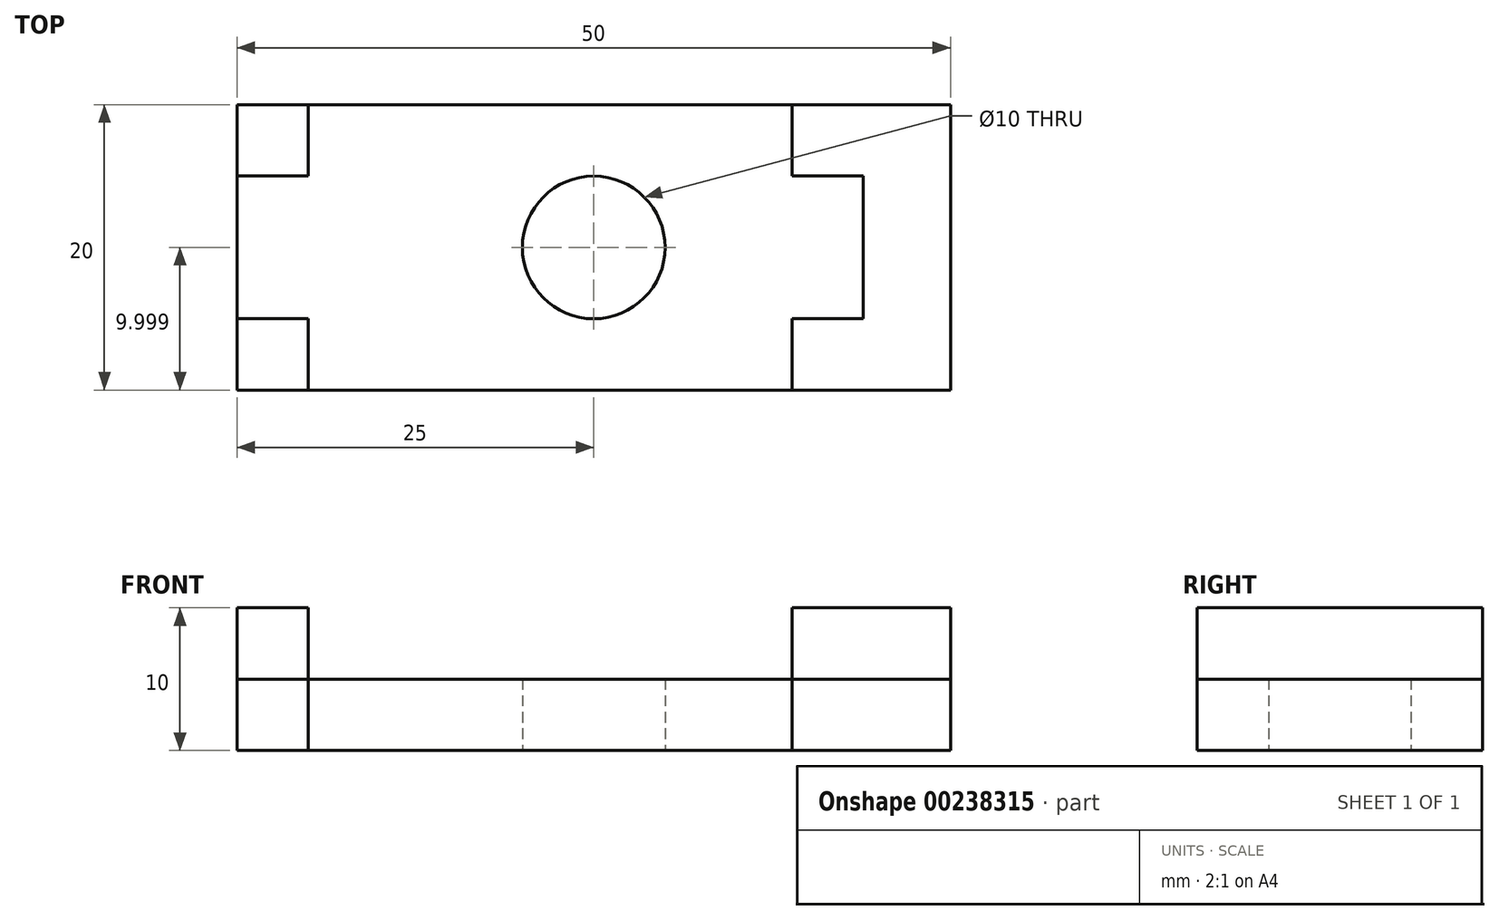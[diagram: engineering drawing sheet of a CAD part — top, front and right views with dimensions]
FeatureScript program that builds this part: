
annotation { "Feature Type Name" : "Feature", "Feature Type Description" : "" }
export const myFeature = defineFeature(function(context is Context, id is Id, definition is map)
    precondition{}
    {
        {
            var Q0;
            Q0=qCreatedBy(makeId("Top.planeOp"),FACE);
            var sketch = newSketch(context, id + "F0", { "sketchPlane" : qUnion([Q0])});
            skLineSegment(sketch, "E0.bottom", {"start": v(-21.46, 12.43) * mm, "end": v(28.54, 12.43) * mm});
            skLineSegment(sketch, "E0.top", {"start": v(-21.46, -7.57) * mm, "end": v(28.54, -7.57) * mm});
            skLineSegment(sketch, "E0.left", {"start": v(-21.46, 12.43) * mm, "end": v(-21.46, -7.57) * mm});
            skLineSegment(sketch, "E0.right", {"start": v(28.54, 12.43) * mm, "end": v(28.54, -7.57) * mm});
            skLineSegment(sketch, "E1", {"start": v(3.54, 12.43) * mm, "end": v(3.54, -7.57) * mm, "construction": true});
            skLineSegment(sketch, "E2", {"start": v(-21.46, 2.43) * mm, "end": v(28.54, 2.43) * mm, "construction": true});
            skCircle(sketch, "E3", {"center": v(3.54, 2.43) * mm, "radius": 5 * mm});
            skLineSegment(sketch, "E4", {"start": v(-21.46, 7.43) * mm, "end": v(-16.46, 7.43) * mm});
            skLineSegment(sketch, "E5", {"start": v(-16.46, 7.43) * mm, "end": v(-16.46, 12.43) * mm});
            skLineSegment(sketch, "E6", {"start": v(-16.46, -7.57) * mm, "end": v(-16.46, -2.57) * mm});
            skLineSegment(sketch, "E7", {"start": v(-16.46, -2.57) * mm, "end": v(-21.46, -2.57) * mm});
            skLineSegment(sketch, "E8", {"start": v(17.44, 12.43) * mm, "end": v(17.44, 7.43) * mm});
            skLineSegment(sketch, "E9", {"start": v(17.44, 7.43) * mm, "end": v(22.44, 7.43) * mm});
            skLineSegment(sketch, "E10", {"start": v(22.44, 7.43) * mm, "end": v(22.44, -2.57) * mm});
            skLineSegment(sketch, "E11", {"start": v(22.44, -2.57) * mm, "end": v(17.44, -2.57) * mm});
            skLineSegment(sketch, "E12", {"start": v(17.44, -2.57) * mm, "end": v(17.44, -7.57) * mm});
            skSolve(sketch);
        }
        {
            var Q0;
            {var subQ4=sQuery(id+"F0.wireOp",EDGE,"E4");Q0=makeQuery(id+"F0.imprint","IMPRINT",FACE,{"disambiguationData":[TD([[makeQuery(id+"F0.imprint","IMPRINT",EDGE,{"derivedFrom":subQ4}),1.0]])]});}
            var Q1;
            {var subQ1=sQuery(id+"F0.wireOp",EDGE,"E0.right");Q1=makeQuery(id+"F0.imprint","IMPRINT",FACE,{"disambiguationData":[TD([[makeQuery(id+"F0.imprint","IMPRINT",EDGE,{"derivedFrom":subQ1}),-1.0]])]});}
            var Q2;
            {var subQ3=sQuery(id+"F0.wireOp",EDGE,"E6");Q2=makeQuery(id+"F0.imprint","IMPRINT",FACE,{"disambiguationData":[TD([[makeQuery(id+"F0.imprint","IMPRINT",EDGE,{"derivedFrom":subQ3}),1.0]])]});}
            extrude(context, id + "F1", {"entities" : qUnion([Q0, Q1, Q2]), "depth" : 10 * mm});
        }
        {
            var Q0;
            Q0 = qSketchRegion(id + "F0", true);
            extrude(context, id + "F2", {"entities" : qUnion([Q0]), "depth" : 5 * mm});
        }
    });
